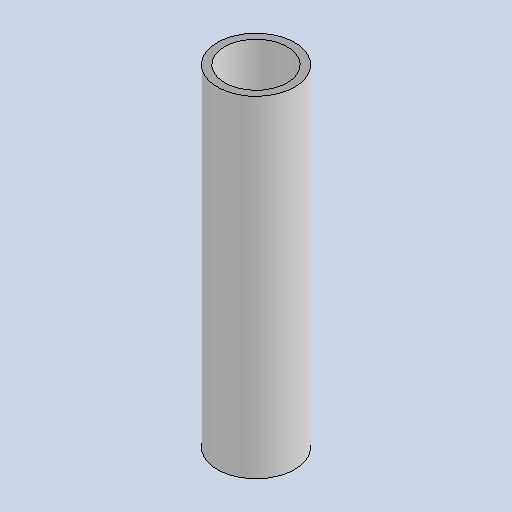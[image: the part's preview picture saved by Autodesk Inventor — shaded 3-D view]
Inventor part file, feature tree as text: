
AUTODESK INVENTOR PART (.ipt)
format: ipt  version: 2025.1 (Build 291241020, 241B)  size: 119,808 bytes
history: native  units: mm
features: extrude x1, sketch x1
ambient origin geometry x8: Origin, YZ Plane, XZ Plane, XY Plane, X Axis, Y Axis, Z Axis, Center Point
bodies: Body1 (feature_tree)
feature tree (2):
  extrude  "Extrusion5"  Depth=90.0mm
  sketch  "Sketch11"  dims[d187=21.0mm d188=2.0mm d189=90.0mm d190=0.0mm]
